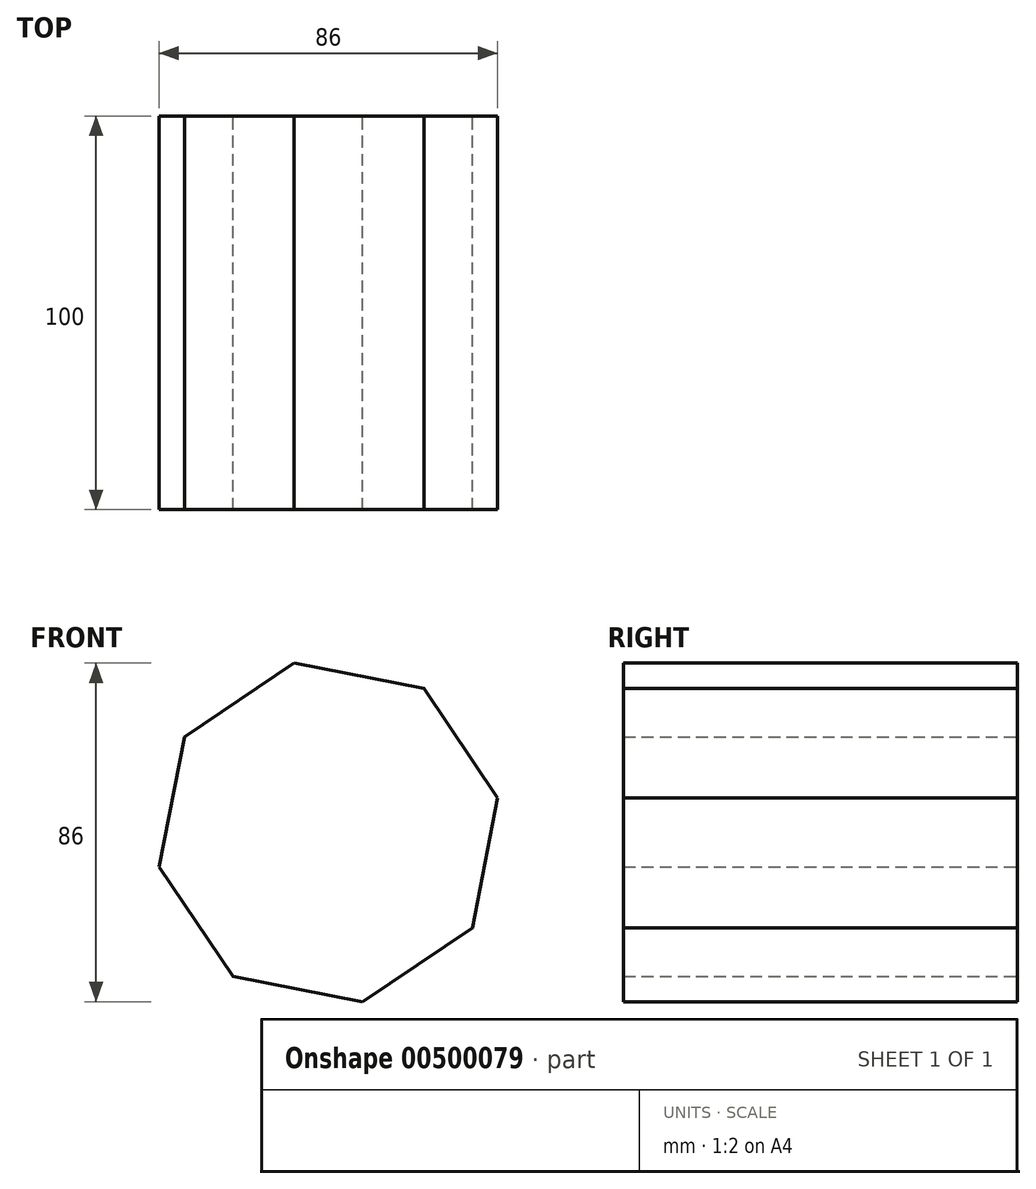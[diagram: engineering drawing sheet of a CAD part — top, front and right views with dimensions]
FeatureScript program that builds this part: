
annotation { "Feature Type Name" : "Feature", "Feature Type Description" : "" }
export const myFeature = defineFeature(function(context is Context, id is Id, definition is map)
    precondition{}
    {
        {
            var Q0;
            Q0=qCreatedBy(makeId("Front.planeOp"),FACE);
            var sketch = newSketch(context, id + "F0", { "sketchPlane" : qUnion([Q0])});
            skCircle(sketch, "E0.cCircle", {"center": v(0, 0) * mm, "radius": 43.87 * mm, "construction": true});
            skLineSegment(sketch, "E0.0", {"start": v(36.58, -24.23) * mm, "end": v(8.73, -43) * mm});
            skLineSegment(sketch, "E0.1", {"start": v(8.73, -43) * mm, "end": v(-24.23, -36.58) * mm});
            skLineSegment(sketch, "E0.2", {"start": v(-24.23, -36.58) * mm, "end": v(-43, -8.73) * mm});
            skLineSegment(sketch, "E0.3", {"start": v(-43, -8.73) * mm, "end": v(-36.58, 24.23) * mm});
            skLineSegment(sketch, "E0.4", {"start": v(-36.58, 24.23) * mm, "end": v(-8.73, 43) * mm});
            skLineSegment(sketch, "E0.5", {"start": v(-8.73, 43) * mm, "end": v(24.23, 36.58) * mm});
            skLineSegment(sketch, "E0.6", {"start": v(24.23, 36.58) * mm, "end": v(43, 8.73) * mm});
            skLineSegment(sketch, "E0.7", {"start": v(43, 8.73) * mm, "end": v(36.58, -24.23) * mm});
            skSolve(sketch);
        }
        {
            var Q0;
            Q0=makeQuery(id+"F0.imprint","IMPRINT",FACE,{"disambiguationData":[TD([[makeQuery(id+"F0.imprint","IMPRINT",EDGE,{"derivedFrom":sQuery(id+"F0.wireOp",EDGE,"E0.0")}),-1.0]])]});
            extrude(context, id + "F1", {"entities" : qUnion([Q0]), "endBound" : BoundingType.SYMMETRIC, "depth" : 100 * mm});
        }
    });
